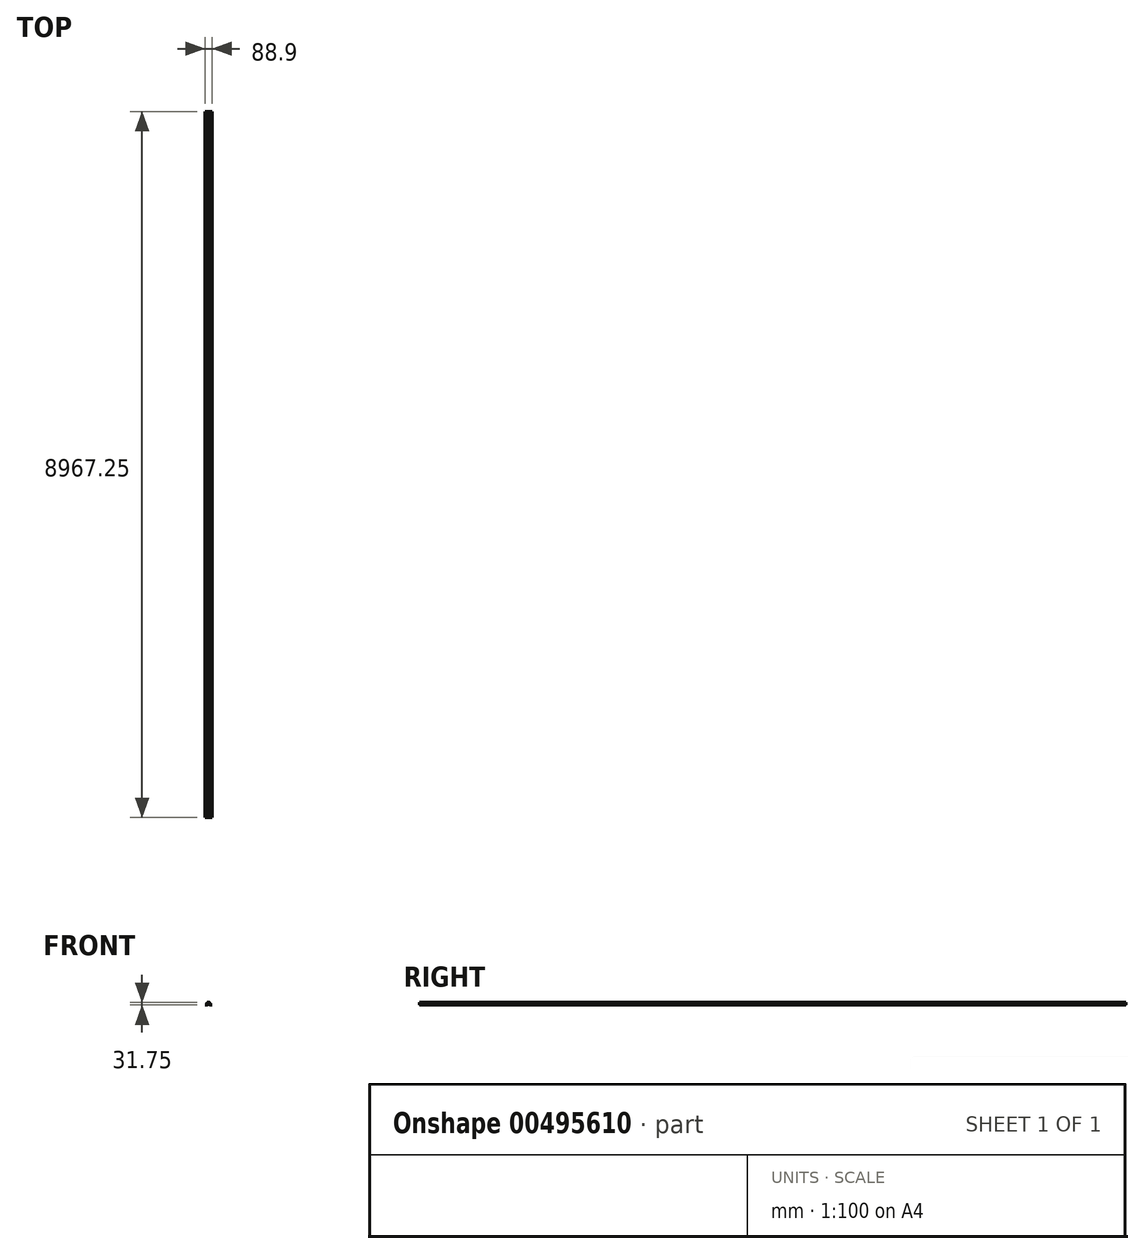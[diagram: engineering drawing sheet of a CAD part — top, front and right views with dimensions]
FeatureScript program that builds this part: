
annotation { "Feature Type Name" : "Feature", "Feature Type Description" : "" }
export const myFeature = defineFeature(function(context is Context, id is Id, definition is map)
    precondition{}
    {
        {
            var Q0;
            Q0=qCreatedBy(makeId("Front.planeOp"),FACE);
            var sketch = newSketch(context, id + "F0", { "sketchPlane" : qUnion([Q0])});
            skLineSegment(sketch, "E0", {"start": v(0, 0) * mm, "end": v(29.25, 0) * mm});
            skPoint(sketch, "E1", {"position": v(0, 31.75) * mm});
            skPoint(sketch, "E2", {"position": v(28.57, 31.75) * mm});
            skPoint(sketch, "E3", {"position": v(60.32, 31.75) * mm});
            skLineSegment(sketch, "E4", {"start": v(31.07, 31.75) * mm, "end": v(57.83, 31.75) * mm});
            skLineSegment(sketch, "E5", {"start": v(0, 0) * mm, "end": v(0, 3.17) * mm});
            skLineSegment(sketch, "E6", {"start": v(0, 3.17) * mm, "end": v(26.07, 3.17) * mm});
            skLineSegment(sketch, "E7", {"start": v(28.57, 5.67) * mm, "end": v(28.57, 29.25) * mm});
            skLineSegment(sketch, "E8", {"start": v(60.32, 29.25) * mm, "end": v(60.32, 5.67) * mm});
            skLineSegment(sketch, "E9", {"start": v(59.65, 0) * mm, "end": v(88.9, 0) * mm});
            skLineSegment(sketch, "E10", {"start": v(31.75, 2.5) * mm, "end": v(31.75, 26.08) * mm});
            skLineSegment(sketch, "E11", {"start": v(34.25, 28.58) * mm, "end": v(54.65, 28.58) * mm});
            skLineSegment(sketch, "E12", {"start": v(57.15, 26.08) * mm, "end": v(57.15, 2.5) * mm});
            skLineSegment(sketch, "E13", {"start": v(62.83, 3.18) * mm, "end": v(88.9, 3.18) * mm});
            skLineSegment(sketch, "E14", {"start": v(88.9, 3.18) * mm, "end": v(88.9, 0) * mm});
            skArc(sketch, "E15.filletArc", {"start": v(31.07, 31.75) * mm, "mid": v(29.3, 31.02) * mm, "end": v(28.57, 29.25) * mm});
            skArc(sketch, "E16.filletArc", {"start": v(60.33, 29.25) * mm, "mid": v(59.6, 31.02) * mm, "end": v(57.83, 31.75) * mm});
            skPoint(sketch, "E17.visualSharp", {"position": v(57.15, 28.58) * mm});
            skArc(sketch, "E17.filletArc", {"start": v(57.15, 26.08) * mm, "mid": v(56.42, 27.84) * mm, "end": v(54.65, 28.58) * mm});
            skPoint(sketch, "E18.visualSharp", {"position": v(31.75, 28.58) * mm});
            skArc(sketch, "E18.filletArc", {"start": v(34.25, 28.58) * mm, "mid": v(32.48, 27.84) * mm, "end": v(31.75, 26.08) * mm});
            skPoint(sketch, "E19.visualSharp", {"position": v(57.15, 0) * mm});
            skArc(sketch, "E19.filletArc", {"start": v(57.15, 2.5) * mm, "mid": v(57.88, 0.73) * mm, "end": v(59.65, 0) * mm});
            skPoint(sketch, "E20.visualSharp", {"position": v(60.32, 3.18) * mm});
            skArc(sketch, "E20.filletArc", {"start": v(60.33, 5.67) * mm, "mid": v(61.06, 3.9) * mm, "end": v(62.83, 3.17) * mm});
            skPoint(sketch, "E21.visualSharp", {"position": v(28.57, 3.18) * mm});
            skArc(sketch, "E21.filletArc", {"start": v(26.07, 3.18) * mm, "mid": v(27.84, 3.9) * mm, "end": v(28.57, 5.68) * mm});
            skPoint(sketch, "E22.visualSharp", {"position": v(31.75, 0) * mm});
            skArc(sketch, "E22.filletArc", {"start": v(29.25, 0) * mm, "mid": v(31.02, 0.73) * mm, "end": v(31.75, 2.5) * mm});
            skSolve(sketch);
        }
        {
            var Q0;
            Q0=makeQuery(id+"F0.imprint","IMPRINT",FACE,{"disambiguationData":[TD([[makeQuery(id+"F0.imprint","IMPRINT",EDGE,{"derivedFrom":sQuery(id+"F0.wireOp",EDGE,"E0")}),1.0]])]});
            extrude(context, id + "F1", {"entities" : qUnion([Q0]), "depth" : 8967.25 * mm});
        }
    });
